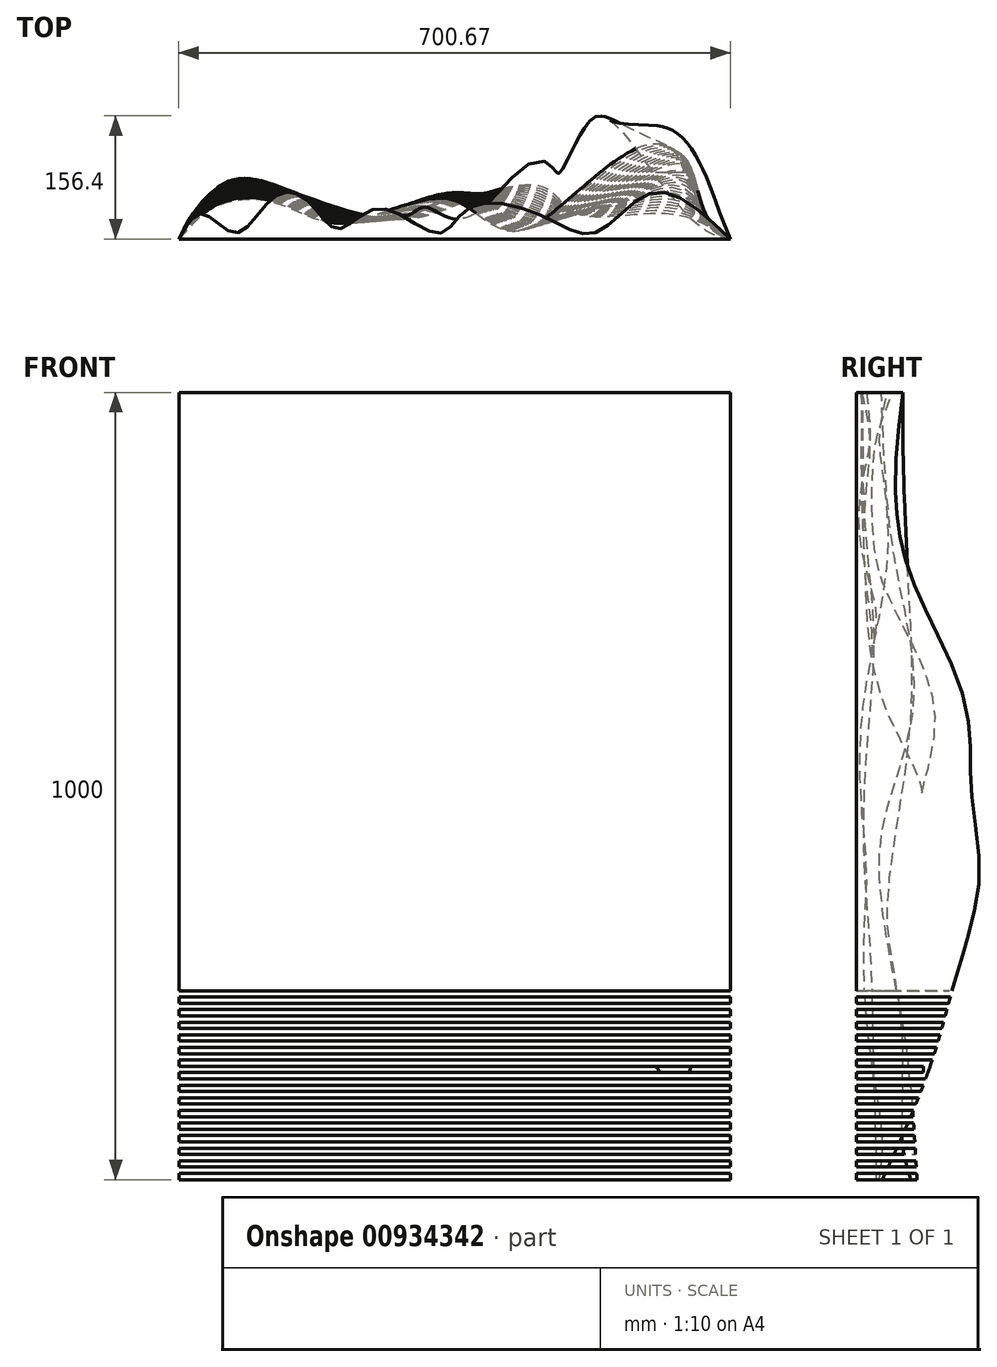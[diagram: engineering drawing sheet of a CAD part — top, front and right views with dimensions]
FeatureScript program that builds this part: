
annotation { "Feature Type Name" : "Feature", "Feature Type Description" : "" }
export const myFeature = defineFeature(function(context is Context, id is Id, definition is map)
    precondition{}
    {
        {
            var Q0;
            Q0=qCreatedBy(makeId("Top.planeOp"),FACE);
            var sketch = newSketch(context, id + "F0", { "sketchPlane" : qUnion([Q0])});
            skLineSegment(sketch, "E0", {"start": v(350, 0) * mm, "end": v(-350, 0) * mm});
            skFitSpline(sketch, "E1", {"points": [v(-350, 0) * mm, v(-285.73, 73.82) * mm, v(-206.35, 60.2) * mm, v(-75.17, 25.13) * mm, v(-1.55, 41.96) * mm, v(59.92, 64.08) * mm, v(117.13, 64.08) * mm, v(153.64, 32.44) * mm, v(271.7, 32.44) * mm, v(350, 0) * mm], "startDerivative": vector(350.32, 778.3) * mm, "endDerivative": vector(622.05, -372.24) * mm});
            skSolve(sketch);
        }
        {
            var Q0;
            Q0=makeQuery(id+"F0.imprint","IMPRINT",FACE,{"disambiguationData":[TD([[makeQuery(id+"F0.imprint","IMPRINT",EDGE,{"derivedFrom":sQuery(id+"F0.wireOp",EDGE,"E0")}),-1.0]])]});
            cPlane(context, id + "F1", {"entities" : qUnion([Q0]), "cplaneType" : CPlaneType.OFFSET, "offset" : 200 * mm, "width" : 150 * mm, "height" : 150 * mm});
        }
        {
            var Q0;
            Q0=qCreatedBy(id+"F1.planeOp",FACE);
            var sketch = newSketch(context, id + "F2", { "sketchPlane" : qUnion([Q0])});
            skLineSegment(sketch, "E2", {"start": v(-350, 0) * mm, "end": v(350, 0) * mm});
            skFitSpline(sketch, "E3", {"points": [v(-350, 0) * mm, v(-305.08, 49) * mm, v(-228.8, 52.95) * mm, v(-144.63, 21.38) * mm, v(-73.6, 37.16) * mm, v(0, 55.58) * mm, v(55.28, 22.7) * mm, v(115.77, 21.38) * mm, v(285.85, 108.51) * mm, v(350, 0) * mm], "startDerivative": vector(398.41, 606.78) * mm, "endDerivative": vector(1198.63, -396.34) * mm});
            skSolve(sketch);
        }
        {
            var Q0;
            Q0=makeQuery(id+"F2.imprint","IMPRINT",FACE,{"disambiguationData":[TD([[makeQuery(id+"F2.imprint","IMPRINT",EDGE,{"derivedFrom":sQuery(id+"F2.wireOp",EDGE,"E2")}),1.0]])]});
            cPlane(context, id + "F3", {"entities" : qUnion([Q0]), "cplaneType" : CPlaneType.OFFSET, "offset" : 200 * mm, "width" : 150 * mm, "height" : 150 * mm});
        }
        {
            var Q0;
            Q0=qCreatedBy(id+"F3.planeOp",FACE);
            var sketch = newSketch(context, id + "F4", { "sketchPlane" : qUnion([Q0])});
            skLineSegment(sketch, "E4", {"start": v(-350, 0) * mm, "end": v(350, 0) * mm});
            skFitSpline(sketch, "E5", {"points": [v(-350, 0) * mm, v(-312.78, 16.87) * mm, v(-251, 28.17) * mm, v(-186.37, 10.35) * mm, v(-143.4, 40.59) * mm, v(-39.04, 26.2) * mm, v(13.5, 12.53) * mm, v(124.25, 69.18) * mm, v(188.04, 155.79) * mm, v(350, 0) * mm], "startDerivative": vector(814.37, 382.43) * mm, "endDerivative": vector(1056.06, -62.09) * mm});
            skSolve(sketch);
        }
        {
            var Q0;
            Q0=qCreatedBy(id+"F3.planeOp",FACE);
            cPlane(context, id + "F5", {"entities" : qUnion([Q0]), "cplaneType" : CPlaneType.OFFSET, "offset" : 200 * mm, "width" : 150 * mm, "height" : 150 * mm});
        }
        {
            var Q0;
            Q0=qCreatedBy(id+"F5.planeOp",FACE);
            var sketch = newSketch(context, id + "F6", { "sketchPlane" : qUnion([Q0])});
            skLineSegment(sketch, "E6", {"start": v(-350, 0) * mm, "end": v(350, 0) * mm});
            skFitSpline(sketch, "E7", {"points": [v(-350, 0) * mm, v(-311.54, 72.16) * mm, v(-252.28, 38.2) * mm, v(-186.23, 21.2) * mm, v(-140.23, 67.63) * mm, v(-71.92, 46.87) * mm, v(-38.33, 14.04) * mm, v(14.5, 19.7) * mm, v(111.23, 98.24) * mm, v(158.3, 36.68) * mm, v(269.26, 139.33) * mm, v(350, 0) * mm], "startDerivative": vector(337.77, 1071.33) * mm, "endDerivative": vector(649, -751.58) * mm});
            skSolve(sketch);
        }
        {
            var Q0;
            Q0=qCreatedBy(id+"F5.planeOp",FACE);
            cPlane(context, id + "F7", {"entities" : qUnion([Q0]), "cplaneType" : CPlaneType.OFFSET, "offset" : 200 * mm, "width" : 150 * mm, "height" : 150 * mm});
        }
        {
            var Q0;
            Q0=qCreatedBy(id+"F7.planeOp",FACE);
            var sketch = newSketch(context, id + "F8", { "sketchPlane" : qUnion([Q0])});
            skLineSegment(sketch, "E8", {"start": v(-350, 0) * mm, "end": v(350, 0) * mm});
            skFitSpline(sketch, "E9", {"points": [v(-350, 0) * mm, v(-342.43, 46.75) * mm, v(-276.97, 13.57) * mm, v(-207.91, 51.68) * mm, v(-146.48, 56.62) * mm, v(-75.19, 9.09) * mm, v(-39.76, 40.02) * mm, v(16.74, 8.19) * mm, v(117.18, 23.43) * mm, v(200.58, 10.88) * mm, v(301.47, 58.86) * mm, v(350, 0) * mm], "startDerivative": vector(-43.86, 939.62) * mm, "endDerivative": vector(428.75, -950.7) * mm});
            skSolve(sketch);
        }
        {
            var Q0;
            Q0=qCreatedBy(id+"F7.planeOp",FACE);
            cPlane(context, id + "F9", {"entities" : qUnion([Q0]), "cplaneType" : CPlaneType.OFFSET, "offset" : 200 * mm, "width" : 150 * mm, "height" : 150 * mm});
        }
        {
            var Q0;
            Q0=qCreatedBy(id+"F9.planeOp",FACE);
            var sketch = newSketch(context, id + "F10", { "sketchPlane" : qUnion([Q0])});
            skLineSegment(sketch, "E10", {"start": v(-350, 0) * mm, "end": v(350, 0) * mm});
            skFitSpline(sketch, "E11", {"points": [v(-350, 0) * mm, v(-320.28, 32.02) * mm, v(-278.07, 7.9) * mm, v(-228.63, 54.13) * mm, v(-186.42, 48.1) * mm, v(-148.23, 13.13) * mm, v(-95.57, 38.86) * mm, v(-20.8, 7.1) * mm, v(19, 40.06) * mm, v(116.28, 27.2) * mm, v(178.59, 7.9) * mm, v(251.35, 58.55) * mm, v(350, 0) * mm], "startDerivative": vector(397.12, 749.22) * mm, "endDerivative": vector(932.12, -893.21) * mm});
            skSolve(sketch);
        }
        {
            var Q0;
            Q0=makeQuery(id+"F0.imprint","IMPRINT",FACE,{"disambiguationData":[TD([[makeQuery(id+"F0.imprint","IMPRINT",EDGE,{"derivedFrom":sQuery(id+"F0.wireOp",EDGE,"E0")}),-1.0]])]});
            var Q1;
            Q1=makeQuery(id+"F2.imprint","IMPRINT",FACE,{"disambiguationData":[TD([[makeQuery(id+"F2.imprint","IMPRINT",EDGE,{"derivedFrom":sQuery(id+"F2.wireOp",EDGE,"E2")}),1.0]])]});
            var Q2;
            Q2=makeQuery(id+"F4.imprint","IMPRINT",FACE,{"disambiguationData":[TD([[makeQuery(id+"F4.imprint","IMPRINT",EDGE,{"derivedFrom":sQuery(id+"F4.wireOp",EDGE,"E4")}),1.0]])]});
            var Q3;
            Q3=makeQuery(id+"F6.imprint","IMPRINT",FACE,{"disambiguationData":[TD([[makeQuery(id+"F6.imprint","IMPRINT",EDGE,{"derivedFrom":sQuery(id+"F6.wireOp",EDGE,"E6")}),1.0]])]});
            var Q4;
            Q4=makeQuery(id+"F8.imprint","IMPRINT",FACE,{"disambiguationData":[TD([[makeQuery(id+"F8.imprint","IMPRINT",EDGE,{"derivedFrom":sQuery(id+"F8.wireOp",EDGE,"E8")}),1.0]])]});
            var Q5;
            Q5=makeQuery(id+"F10.imprint","IMPRINT",FACE,{"disambiguationData":[TD([[makeQuery(id+"F10.imprint","IMPRINT",EDGE,{"derivedFrom":sQuery(id+"F10.wireOp",EDGE,"E10")}),1.0]])]});
            loft(context, id + "F11", {"sheetProfilesArray" : [{ "sheetProfileEntities" : qUnion([Q0]) }, { "sheetProfileEntities" : qUnion([Q1]) }, { "sheetProfileEntities" : qUnion([Q2]) }, { "sheetProfileEntities" : qUnion([Q3]) }, { "sheetProfileEntities" : qUnion([Q4]) }, { "sheetProfileEntities" : qUnion([Q5]) }]});
        }
        {
            var Q0;
            Q0=qCreatedBy(makeId("Top.planeOp"),FACE);
            cPlane(context, id + "F12", {"entities" : qUnion([Q0]), "cplaneType" : CPlaneType.OFFSET, "offset" : 8 * mm, "width" : 150 * mm, "height" : 150 * mm});
        }
        {
            var Q0;
            Q0=qCreatedBy(id+"F12.planeOp",FACE);
            var sketch = newSketch(context, id + "F13", { "sketchPlane" : qUnion([Q0])});
            skLineSegment(sketch, "E12.bottom", {"start": v(-475.83, -96.54) * mm, "end": v(423.7, -96.54) * mm});
            skLineSegment(sketch, "E12.top", {"start": v(-475.83, 169.42) * mm, "end": v(423.7, 169.42) * mm});
            skLineSegment(sketch, "E12.left", {"start": v(-475.83, -96.54) * mm, "end": v(-475.83, 169.42) * mm});
            skLineSegment(sketch, "E12.right", {"start": v(423.7, -96.54) * mm, "end": v(423.7, 169.42) * mm});
            skSolve(sketch);
        }
        {
            var Q0;
            Q0=makeQuery(id+"F13.imprint","IMPRINT",FACE,{"disambiguationData":[TD([[makeQuery(id+"F13.imprint","IMPRINT",EDGE,{"derivedFrom":sQuery(id+"F13.wireOp",EDGE,"E12.bottom")}),1.0]])]});
            extrude(context, id + "F14", {"entities" : qUnion([Q0]), "operationType" : NewBodyOperationType.REMOVE, "depth" : 8 * mm, "offsetDistance" : 25 * mm});
        }
        {
            var Q0;
            Q0=qCreatedBy(id+"F12.planeOp",FACE);
            cPlane(context, id + "F15", {"entities" : qUnion([Q0]), "cplaneType" : CPlaneType.OFFSET, "offset" : 16 * mm, "width" : 150 * mm, "height" : 150 * mm});
        }
        {
            var Q0;
            Q0=qCreatedBy(id+"F15.planeOp",FACE);
            var sketch = newSketch(context, id + "F16", { "sketchPlane" : qUnion([Q0])});
            skLineSegment(sketch, "E13.bottom", {"start": v(-406.68, 133.16) * mm, "end": v(391.15, 133.16) * mm});
            skLineSegment(sketch, "E13.top", {"start": v(-406.68, -82.11) * mm, "end": v(391.15, -82.11) * mm});
            skLineSegment(sketch, "E13.left", {"start": v(-406.68, 133.16) * mm, "end": v(-406.68, -82.11) * mm});
            skLineSegment(sketch, "E13.right", {"start": v(391.15, 133.16) * mm, "end": v(391.15, -82.11) * mm});
            skSolve(sketch);
        }
        {
            var Q0;
            Q0=makeQuery(id+"F16.imprint","IMPRINT",FACE,{"disambiguationData":[TD([[makeQuery(id+"F16.imprint","IMPRINT",EDGE,{"derivedFrom":sQuery(id+"F16.wireOp",EDGE,"E13.bottom")}),-1.0]])]});
            extrude(context, id + "F17", {"entities" : qUnion([Q0]), "operationType" : NewBodyOperationType.REMOVE, "depth" : 8 * mm, "offsetDistance" : 25 * mm});
        }
        {
            var Q0;
            Q0=qCreatedBy(id+"F15.planeOp",FACE);
            cPlane(context, id + "F18", {"entities" : qUnion([Q0]), "cplaneType" : CPlaneType.OFFSET, "offset" : 16 * mm, "width" : 150 * mm, "height" : 150 * mm});
        }
        {
            var Q0;
            Q0=qCreatedBy(id+"F18.planeOp",FACE);
            var sketch = newSketch(context, id + "F19", { "sketchPlane" : qUnion([Q0])});
            skLineSegment(sketch, "E14.bottom", {"start": v(-366.74, -55.15) * mm, "end": v(376.63, -55.15) * mm});
            skLineSegment(sketch, "E14.top", {"start": v(-366.74, 150.1) * mm, "end": v(376.63, 150.1) * mm});
            skLineSegment(sketch, "E14.left", {"start": v(-366.74, -55.15) * mm, "end": v(-366.74, 150.1) * mm});
            skLineSegment(sketch, "E14.right", {"start": v(376.63, -55.15) * mm, "end": v(376.63, 150.1) * mm});
            skSolve(sketch);
        }
        {
            var Q0;
            Q0=makeQuery(id+"F19.imprint","IMPRINT",FACE,{"disambiguationData":[TD([[makeQuery(id+"F19.imprint","IMPRINT",EDGE,{"derivedFrom":sQuery(id+"F19.wireOp",EDGE,"E14.bottom")}),1.0]])]});
            extrude(context, id + "F20", {"entities" : qUnion([Q0]), "operationType" : NewBodyOperationType.REMOVE, "depth" : 8 * mm, "offsetDistance" : 25 * mm});
        }
        {
            var Q0;
            Q0=qCreatedBy(id+"F18.planeOp",FACE);
            cPlane(context, id + "F21", {"entities" : qUnion([Q0]), "cplaneType" : CPlaneType.OFFSET, "offset" : 16 * mm, "width" : 150 * mm, "height" : 150 * mm});
        }
        {
            var Q0;
            Q0=qCreatedBy(id+"F21.planeOp",FACE);
            var sketch = newSketch(context, id + "F22", { "sketchPlane" : qUnion([Q0])});
            skLineSegment(sketch, "E15.bottom", {"start": v(369.57, 100.1) * mm, "end": v(-367.12, 100.1) * mm});
            skLineSegment(sketch, "E15.top", {"start": v(369.57, -28.08) * mm, "end": v(-367.12, -28.08) * mm});
            skLineSegment(sketch, "E15.left", {"start": v(369.57, 100.1) * mm, "end": v(369.57, -28.08) * mm});
            skLineSegment(sketch, "E15.right", {"start": v(-367.12, 100.1) * mm, "end": v(-367.12, -28.08) * mm});
            skSolve(sketch);
        }
        {
            var Q0;
            Q0=makeQuery(id+"F22.imprint","IMPRINT",FACE,{"disambiguationData":[TD([[makeQuery(id+"F22.imprint","IMPRINT",EDGE,{"derivedFrom":sQuery(id+"F22.wireOp",EDGE,"E15.bottom")}),1.0]])]});
            extrude(context, id + "F23", {"entities" : qUnion([Q0]), "operationType" : NewBodyOperationType.REMOVE, "depth" : 8 * mm, "offsetDistance" : 25 * mm});
        }
        {
            var Q0;
            Q0=qCreatedBy(id+"F21.planeOp",FACE);
            cPlane(context, id + "F24", {"entities" : qUnion([Q0]), "cplaneType" : CPlaneType.OFFSET, "offset" : 16 * mm, "width" : 150 * mm, "height" : 150 * mm});
        }
        {
            var Q0;
            Q0=qCreatedBy(id+"F24.planeOp",FACE);
            var sketch = newSketch(context, id + "F25", { "sketchPlane" : qUnion([Q0])});
            skLineSegment(sketch, "E16.bottom", {"start": v(-363.47, -19.42) * mm, "end": v(355.58, -19.42) * mm});
            skLineSegment(sketch, "E16.top", {"start": v(-363.47, 89.34) * mm, "end": v(355.58, 89.34) * mm});
            skLineSegment(sketch, "E16.left", {"start": v(-363.47, -19.42) * mm, "end": v(-363.47, 89.34) * mm});
            skLineSegment(sketch, "E16.right", {"start": v(355.58, -19.42) * mm, "end": v(355.58, 89.34) * mm});
            skSolve(sketch);
        }
        {
            var Q0;
            Q0=makeQuery(id+"F25.imprint","IMPRINT",FACE,{"disambiguationData":[TD([[makeQuery(id+"F25.imprint","IMPRINT",EDGE,{"derivedFrom":sQuery(id+"F25.wireOp",EDGE,"E16.bottom")}),1.0]])]});
            extrude(context, id + "F26", {"entities" : qUnion([Q0]), "operationType" : NewBodyOperationType.REMOVE, "depth" : 8 * mm, "offsetDistance" : 25 * mm});
        }
        {
            var Q0;
            Q0=qCreatedBy(id+"F24.planeOp",FACE);
            cPlane(context, id + "F27", {"entities" : qUnion([Q0]), "cplaneType" : CPlaneType.OFFSET, "offset" : 16 * mm, "width" : 150 * mm, "height" : 150 * mm});
        }
        {
            var Q0;
            Q0=qCreatedBy(id+"F27.planeOp",FACE);
            var sketch = newSketch(context, id + "F28", { "sketchPlane" : qUnion([Q0])});
            skLineSegment(sketch, "E17.bottom", {"start": v(-363.3, -11.55) * mm, "end": v(357.63, -11.55) * mm});
            skLineSegment(sketch, "E17.top", {"start": v(-363.3, 87.7) * mm, "end": v(357.63, 87.7) * mm});
            skLineSegment(sketch, "E17.left", {"start": v(-363.3, -11.55) * mm, "end": v(-363.3, 87.7) * mm});
            skLineSegment(sketch, "E17.right", {"start": v(357.63, -11.55) * mm, "end": v(357.63, 87.7) * mm});
            skSolve(sketch);
        }
        {
            var Q0;
            Q0=makeQuery(id+"F28.imprint","IMPRINT",FACE,{"disambiguationData":[TD([[makeQuery(id+"F28.imprint","IMPRINT",EDGE,{"derivedFrom":sQuery(id+"F28.wireOp",EDGE,"E17.bottom")}),1.0]])]});
            extrude(context, id + "F29", {"entities" : qUnion([Q0]), "operationType" : NewBodyOperationType.REMOVE, "depth" : 8 * mm, "offsetDistance" : 25 * mm});
        }
        {
            var Q0;
            Q0=qCreatedBy(id+"F27.planeOp",FACE);
            cPlane(context, id + "F30", {"entities" : qUnion([Q0]), "cplaneType" : CPlaneType.OFFSET, "offset" : 16 * mm, "width" : 150 * mm, "height" : 150 * mm});
        }
        {
            var Q0;
            Q0=qCreatedBy(id+"F30.planeOp",FACE);
            var sketch = newSketch(context, id + "F31", { "sketchPlane" : qUnion([Q0])});
            skLineSegment(sketch, "E18.bottom", {"start": v(-365.74, 0) * mm, "end": v(369.65, 0) * mm});
            skLineSegment(sketch, "E18.top", {"start": v(-365.74, 94.7) * mm, "end": v(369.65, 94.7) * mm});
            skLineSegment(sketch, "E18.left", {"start": v(-365.74, 0) * mm, "end": v(-365.74, 94.7) * mm});
            skLineSegment(sketch, "E18.right", {"start": v(369.65, 0) * mm, "end": v(369.65, 94.7) * mm});
            skSolve(sketch);
        }
        {
            var Q0;
            Q0=makeQuery(id+"F31.imprint","IMPRINT",FACE,{"disambiguationData":[TD([[makeQuery(id+"F31.imprint","IMPRINT",EDGE,{"derivedFrom":sQuery(id+"F31.wireOp",EDGE,"E18.bottom")}),1.0]])]});
            extrude(context, id + "F32", {"entities" : qUnion([Q0]), "operationType" : NewBodyOperationType.REMOVE, "depth" : 8 * mm, "offsetDistance" : 25 * mm});
        }
        {
            var Q0;
            Q0=qCreatedBy(id+"F30.planeOp",FACE);
            cPlane(context, id + "F33", {"entities" : qUnion([Q0]), "cplaneType" : CPlaneType.OFFSET, "offset" : 16 * mm, "width" : 150 * mm, "height" : 150 * mm});
        }
        {
            var Q0;
            Q0=qCreatedBy(id+"F33.planeOp",FACE);
            var sketch = newSketch(context, id + "F34", { "sketchPlane" : qUnion([Q0])});
            skLineSegment(sketch, "E19.bottom", {"start": v(-360.87, 0) * mm, "end": v(359.25, 0) * mm});
            skLineSegment(sketch, "E19.top", {"start": v(-360.87, 91.64) * mm, "end": v(359.25, 91.64) * mm});
            skLineSegment(sketch, "E19.left", {"start": v(-360.87, 0) * mm, "end": v(-360.87, 91.64) * mm});
            skLineSegment(sketch, "E19.right", {"start": v(359.25, 0) * mm, "end": v(359.25, 91.64) * mm});
            skSolve(sketch);
        }
        {
            var Q0;
            Q0=makeQuery(id+"F34.imprint","IMPRINT",FACE,{"disambiguationData":[TD([[makeQuery(id+"F34.imprint","IMPRINT",EDGE,{"derivedFrom":sQuery(id+"F34.wireOp",EDGE,"E19.bottom")}),1.0]])]});
            extrude(context, id + "F35", {"entities" : qUnion([Q0]), "operationType" : NewBodyOperationType.REMOVE, "depth" : 8 * mm, "offsetDistance" : 25 * mm});
        }
        {
            var Q0;
            Q0=qCreatedBy(id+"F33.planeOp",FACE);
            cPlane(context, id + "F36", {"entities" : qUnion([Q0]), "cplaneType" : CPlaneType.OFFSET, "offset" : 16 * mm, "width" : 150 * mm, "height" : 150 * mm});
        }
        {
            var Q0;
            Q0=qCreatedBy(id+"F36.planeOp",FACE);
            var sketch = newSketch(context, id + "F37", { "sketchPlane" : qUnion([Q0])});
            skLineSegment(sketch, "E20.bottom", {"start": v(-372.87, 0) * mm, "end": v(361.12, 0) * mm});
            skLineSegment(sketch, "E20.top", {"start": v(-372.87, 85) * mm, "end": v(361.12, 85) * mm});
            skLineSegment(sketch, "E20.left", {"start": v(-372.87, 0) * mm, "end": v(-372.87, 85) * mm});
            skLineSegment(sketch, "E20.right", {"start": v(361.12, 0) * mm, "end": v(361.12, 85) * mm});
            skSolve(sketch);
        }
        {
            var Q0;
            Q0=makeQuery(id+"F37.imprint","IMPRINT",FACE,{"disambiguationData":[TD([[makeQuery(id+"F37.imprint","IMPRINT",EDGE,{"derivedFrom":sQuery(id+"F37.wireOp",EDGE,"E20.bottom")}),1.0]])]});
            extrude(context, id + "F38", {"entities" : qUnion([Q0]), "operationType" : NewBodyOperationType.REMOVE, "depth" : 8 * mm, "offsetDistance" : 25 * mm});
        }
        {
            var Q0;
            Q0=qCreatedBy(id+"F36.planeOp",FACE);
            cPlane(context, id + "F39", {"entities" : qUnion([Q0]), "cplaneType" : CPlaneType.OFFSET, "offset" : 16 * mm, "width" : 150 * mm, "height" : 150 * mm});
        }
        {
            var Q0;
            Q0=qCreatedBy(id+"F39.planeOp",FACE);
            var sketch = newSketch(context, id + "F40", { "sketchPlane" : qUnion([Q0])});
            skLineSegment(sketch, "E21.bottom", {"start": v(-378.1, -15.02) * mm, "end": v(382.01, -15.02) * mm});
            skLineSegment(sketch, "E21.top", {"start": v(-378.1, 112.97) * mm, "end": v(382.01, 112.97) * mm});
            skLineSegment(sketch, "E21.left", {"start": v(-378.1, -15.02) * mm, "end": v(-378.1, 112.97) * mm});
            skLineSegment(sketch, "E21.right", {"start": v(382.01, -15.02) * mm, "end": v(382.01, 112.97) * mm});
            skSolve(sketch);
        }
        {
            var Q0;
            Q0=makeQuery(id+"F40.imprint","IMPRINT",FACE,{"disambiguationData":[TD([[makeQuery(id+"F40.imprint","IMPRINT",EDGE,{"derivedFrom":sQuery(id+"F40.wireOp",EDGE,"E21.bottom")}),1.0]])]});
            extrude(context, id + "F41", {"entities" : qUnion([Q0]), "operationType" : NewBodyOperationType.REMOVE, "depth" : 8 * mm, "offsetDistance" : 25 * mm});
        }
        {
            var Q0;
            Q0=qCreatedBy(id+"F39.planeOp",FACE);
            cPlane(context, id + "F42", {"entities" : qUnion([Q0]), "cplaneType" : CPlaneType.OFFSET, "offset" : 16 * mm, "width" : 150 * mm, "height" : 150 * mm});
        }
        {
            var Q0;
            Q0=qCreatedBy(id+"F42.planeOp",FACE);
            var sketch = newSketch(context, id + "F43", { "sketchPlane" : qUnion([Q0])});
            skLineSegment(sketch, "E22.bottom", {"start": v(399, -24.16) * mm, "end": v(-368.95, -24.16) * mm});
            skLineSegment(sketch, "E22.top", {"start": v(399, 128.64) * mm, "end": v(-368.95, 128.64) * mm});
            skLineSegment(sketch, "E22.left", {"start": v(399, -24.16) * mm, "end": v(399, 128.64) * mm});
            skLineSegment(sketch, "E22.right", {"start": v(-368.95, -24.16) * mm, "end": v(-368.95, 128.64) * mm});
            skSolve(sketch);
        }
        {
            var Q0;
            Q0=makeQuery(id+"F43.imprint","IMPRINT",FACE,{"disambiguationData":[TD([[makeQuery(id+"F43.imprint","IMPRINT",EDGE,{"derivedFrom":sQuery(id+"F43.wireOp",EDGE,"E22.bottom")}),-1.0]])]});
            extrude(context, id + "F44", {"entities" : qUnion([Q0]), "operationType" : NewBodyOperationType.REMOVE, "depth" : 8 * mm, "offsetDistance" : 25 * mm});
        }
        {
            var Q0;
            Q0=qCreatedBy(id+"F42.planeOp",FACE);
            cPlane(context, id + "F45", {"entities" : qUnion([Q0]), "cplaneType" : CPlaneType.OFFSET, "offset" : 16 * mm, "width" : 150 * mm, "height" : 150 * mm});
        }
        {
            var Q0;
            Q0=qCreatedBy(id+"F45.planeOp",FACE);
            var sketch = newSketch(context, id + "F46", { "sketchPlane" : qUnion([Q0])});
            skLineSegment(sketch, "E23.bottom", {"start": v(393.2, -448.55) * mm, "end": v(-422.28, -448.55) * mm});
            skLineSegment(sketch, "E23.top", {"start": v(393.2, 264.35) * mm, "end": v(-422.28, 264.35) * mm});
            skLineSegment(sketch, "E23.left", {"start": v(393.2, -448.55) * mm, "end": v(393.2, 264.35) * mm});
            skLineSegment(sketch, "E23.right", {"start": v(-422.28, -448.55) * mm, "end": v(-422.28, 264.35) * mm});
            skSolve(sketch);
        }
        {
            var Q0;
            Q0=makeQuery(id+"F46.imprint","IMPRINT",FACE,{"disambiguationData":[TD([[makeQuery(id+"F46.imprint","IMPRINT",EDGE,{"derivedFrom":sQuery(id+"F46.wireOp",EDGE,"E23.bottom")}),-1.0]])]});
            extrude(context, id + "F47", {"entities" : qUnion([Q0]), "operationType" : NewBodyOperationType.REMOVE, "depth" : 8 * mm, "offsetDistance" : 25 * mm});
        }
        {
            var Q0;
            Q0=qCreatedBy(id+"F45.planeOp",FACE);
            cPlane(context, id + "F48", {"entities" : qUnion([Q0]), "cplaneType" : CPlaneType.OFFSET, "offset" : 16 * mm, "width" : 150 * mm, "height" : 150 * mm});
        }
        {
            var Q0;
            Q0=qCreatedBy(id+"F48.planeOp",FACE);
            var sketch = newSketch(context, id + "F49", { "sketchPlane" : qUnion([Q0])});
            skLineSegment(sketch, "E24.bottom", {"start": v(364.43, -300.8) * mm, "end": v(-388.92, -300.8) * mm});
            skLineSegment(sketch, "E24.top", {"start": v(364.43, 237.29) * mm, "end": v(-388.92, 237.29) * mm});
            skLineSegment(sketch, "E24.left", {"start": v(364.43, -300.8) * mm, "end": v(364.43, 237.29) * mm});
            skLineSegment(sketch, "E24.right", {"start": v(-388.92, -300.8) * mm, "end": v(-388.92, 237.29) * mm});
            skSolve(sketch);
        }
        {
            var Q0;
            Q0=makeQuery(id+"F49.imprint","IMPRINT",FACE,{"disambiguationData":[TD([[makeQuery(id+"F49.imprint","IMPRINT",EDGE,{"derivedFrom":sQuery(id+"F49.wireOp",EDGE,"E24.bottom")}),-1.0]])]});
            extrude(context, id + "F50", {"entities" : qUnion([Q0]), "operationType" : NewBodyOperationType.REMOVE, "depth" : 8 * mm, "offsetDistance" : 25 * mm});
        }
        {
            var Q0;
            Q0=qCreatedBy(id+"F48.planeOp",FACE);
            cPlane(context, id + "F51", {"entities" : qUnion([Q0]), "cplaneType" : CPlaneType.OFFSET, "offset" : 16 * mm, "width" : 150 * mm, "height" : 150 * mm});
        }
        {
            var Q0;
            Q0=qCreatedBy(id+"F51.planeOp",FACE);
            var sketch = newSketch(context, id + "F52", { "sketchPlane" : qUnion([Q0])});
            skLineSegment(sketch, "E25.bottom", {"start": v(373.48, -353.5) * mm, "end": v(-396.46, -353.5) * mm});
            skLineSegment(sketch, "E25.top", {"start": v(373.48, 303.17) * mm, "end": v(-396.46, 303.17) * mm});
            skLineSegment(sketch, "E25.left", {"start": v(373.48, -353.5) * mm, "end": v(373.48, 303.17) * mm});
            skLineSegment(sketch, "E25.right", {"start": v(-396.46, -353.5) * mm, "end": v(-396.46, 303.17) * mm});
            skSolve(sketch);
        }
        {
            var Q0;
            Q0=makeQuery(id+"F52.imprint","IMPRINT",FACE,{"disambiguationData":[TD([[makeQuery(id+"F52.imprint","IMPRINT",EDGE,{"derivedFrom":sQuery(id+"F52.wireOp",EDGE,"E25.bottom")}),-1.0]])]});
            extrude(context, id + "F53", {"entities" : qUnion([Q0]), "operationType" : NewBodyOperationType.REMOVE, "depth" : 8 * mm, "offsetDistance" : 25 * mm});
        }
        {
            var Q0;
            Q0=qCreatedBy(id+"F51.planeOp",FACE);
            cPlane(context, id + "F54", {"entities" : qUnion([Q0]), "cplaneType" : CPlaneType.OFFSET, "offset" : 16 * mm, "width" : 150 * mm, "height" : 150 * mm});
        }
        {
            var Q0;
            Q0=qCreatedBy(id+"F54.planeOp",FACE);
            var sketch = newSketch(context, id + "F55", { "sketchPlane" : qUnion([Q0])});
            skLineSegment(sketch, "E26.bottom", {"start": v(392.33, -287.19) * mm, "end": v(-400.85, -287.19) * mm});
            skLineSegment(sketch, "E26.top", {"start": v(392.33, 206.73) * mm, "end": v(-400.85, 206.73) * mm});
            skLineSegment(sketch, "E26.left", {"start": v(392.33, -287.19) * mm, "end": v(392.33, 206.73) * mm});
            skLineSegment(sketch, "E26.right", {"start": v(-400.85, -287.19) * mm, "end": v(-400.85, 206.73) * mm});
            skSolve(sketch);
        }
        {
            var Q0;
            Q0=makeQuery(id+"F55.imprint","IMPRINT",FACE,{"disambiguationData":[TD([[makeQuery(id+"F55.imprint","IMPRINT",EDGE,{"derivedFrom":sQuery(id+"F55.wireOp",EDGE,"E26.bottom")}),-1.0]])]});
            extrude(context, id + "F56", {"entities" : qUnion([Q0]), "operationType" : NewBodyOperationType.REMOVE, "depth" : 8 * mm, "offsetDistance" : 25 * mm});
        }
    });
